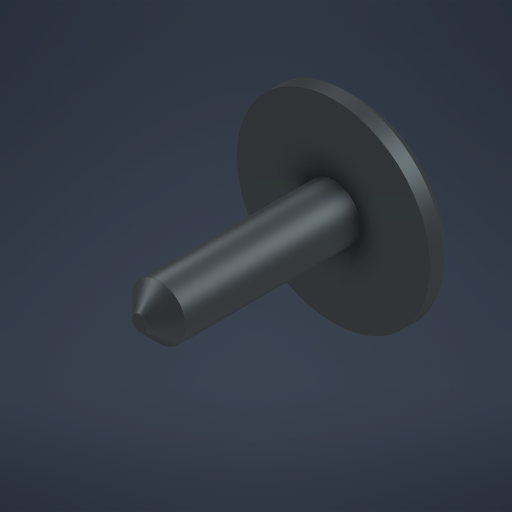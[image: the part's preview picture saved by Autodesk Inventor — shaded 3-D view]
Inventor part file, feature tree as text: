
AUTODESK INVENTOR PART (.ipt)
format: ipt  version: 2023 (Build 270158000, 158)  size: 290,816 bytes
history: native  units: mm
features: chamfer x5, extrude x3, sketch x3, fillet x1
ambient origin geometry x8: Origin, YZ Plane, XZ Plane, XY Plane, X Axis, Y Axis, Z Axis, Center Point
bodies: Solid1 (feature_tree)
feature tree (12):
  extrude  "Extrusion1"  Depth=2.0mm TaperAngle=0.0deg
  extrude  "Extrusion2"  Depth=10.0mm TaperAngle=0.0deg
  chamfer  "Chamfer1"  Distance=1.0mm Angle=45.0deg
  chamfer  "Chamfer2"  Distance=1.3mm Angle=45.0deg
  fillet  "Fillet1"  Radius=3.0mm
  extrude  "Extrusion3"  Depth=1.0mm
  chamfer  "Chamfer3"  Distance=1.0mm
  chamfer  "Chamfer4"  Distance=0.5mm Angle=45.0deg
  chamfer  "Chamfer5"  Distance=0.5mm Angle=45.0deg
  sketch  "Sketch1"  dims[d0=10.0mm d1=2.0mm d2=0.0mm]
  sketch  "Sketch2"  dims[d3=2.8mm d4=10.0mm d5=0.0mm d6=1.0mm d7=2.0mm d8=45.0deg d9=1.3mm d10=2.0mm d11=45.0deg d12=3.0mm]
  sketch  "Sketch3"  dims[d15=6.0mm d16=1.0mm d17=1.0mm d18=0.0mm d19=0.5mm d20=2.0mm d21=45.0deg d22=0.5mm d23=2.0mm d24=45.0deg d25=0.5mm d26=2.0mm d27=45.0deg]
